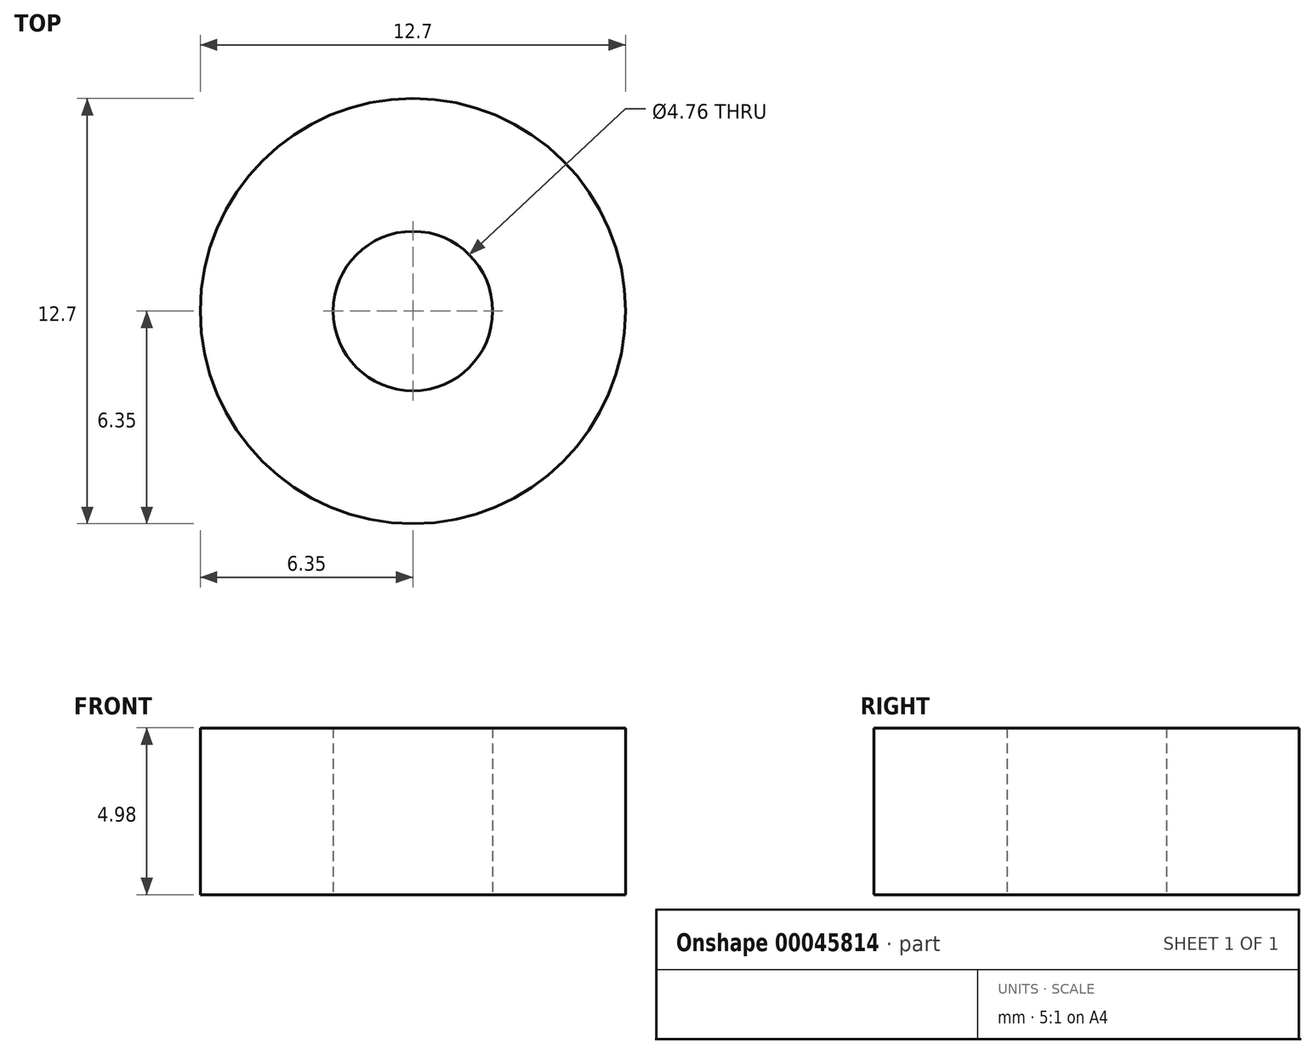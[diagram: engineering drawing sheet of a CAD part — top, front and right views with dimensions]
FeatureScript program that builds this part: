
annotation { "Feature Type Name" : "Feature", "Feature Type Description" : "" }
export const myFeature = defineFeature(function(context is Context, id is Id, definition is map)
    precondition{}
    {
        {
            var Q0;
            Q0=qCreatedBy(makeId("Top.planeOp"),FACE);
            var sketch = newSketch(context, id + "F0", { "sketchPlane" : qUnion([Q0])});
            skCircle(sketch, "E0", {"center": v(0, 0) * mm, "radius": 6.35 * mm});
            skCircle(sketch, "E1", {"center": v(0, 0) * mm, "radius": 2.38 * mm});
            skSolve(sketch);
        }
        {
            var Q0;
            Q0=qSketchRegion(id+"F0",true);
            extrude(context, id + "F1", {"entities" : qUnion([Q0]), "depth" : 4.98 * mm});
        }
    });
